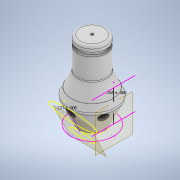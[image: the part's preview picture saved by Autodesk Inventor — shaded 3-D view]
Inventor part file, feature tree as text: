
AUTODESK INVENTOR PART (.ipt)
format: ipt  version: 2020 (Build 240168000, 168)  size: 306,176 bytes
history: native  units: in
note: dims shown in document units (in); Inventor stores cm internally (conversion verified against a paired STEP export)
features: sketch x6, hole x4, plane x2, fillet x2, revolve x1, pattern_circular x1
ambient origin geometry x8: Origin, YZ Plane, XZ Plane, XY Plane, X Axis, Y Axis, Z Axis, Center Point
bodies: Solid1 (feature_tree)
feature tree (16):
  revolve  "Revolution1"  [1 undecoded]
  hole  "Hole4"  [1 undecoded]
  hole  "Hole8"  [1 undecoded]
  sketch  "Sketch13"  dims[d2=90.0deg d3=0.057in]
  plane  "Work Plane6"
  sketch  "Sketch14"  dims[d4=0.095in d5=0.125in]
  sketch  "Sketch29"  dims[d24=0.4466in d25=0.125in]
  plane  "Work Plane5"
  sketch  "Sketch30"  dims[d54=0.3779in d72=0.3779in d83=0.75in d84=0.75in d85=0.0625in d86=0.75in d87=0.375in d88=0.25in d89=0.5635in d90=1.1in d91=0.8108in d92=0.2645in d121=0.196in d122=0.25in d123=0.375in d124=0.25in d125=0.5635in d126=0.25in d127=0.0in d137=0.3779in d155=0.3779in d173=0.3779in d191=0.3779in d221=0.3779in d239=0.3779in d253=0.4466in d254=0.1325in d255=0.0625in d256=0.25in d257=0.375in d258=0.25in d259=0.5635in d260=0.55in d261=0.0in d262=0.211in d263=0.2in d264=0.375in d265=0.25in d266=0.5635in d267=0.25in d268=0.0in d269=1.5748in d270=1.3743in d272=0.0625in d273=0.0625in d274=1.0in d275=1.0in d276=1.0in d277=0.15in d278=0.25in d279=0.375in d280=0.5635in d281=0.75in d282=0.8108in d283=0.0625in d284=0.75in d285=0.375in]
  hole  "Hole9"  [1 undecoded]
  hole  "Hole10"  [1 undecoded]
  pattern_circular  "Circular Pattern7"  [2 undecoded]
  fillet  "Fillet1"  Radius=0.75in
  fillet  "Fillet2"  Radius=0.75in
  sketch  "Sketch12"  dims[d0=0.3328in d1=0.5in]
  sketch  "Sketch16"  dims[d6=90.0deg d23=0.65in]
note: 7 required parameter values undecoded (feature->parameter linkage not recoverable at this tier; creation-order binding heuristic only, values carry confidence <= 0.55)